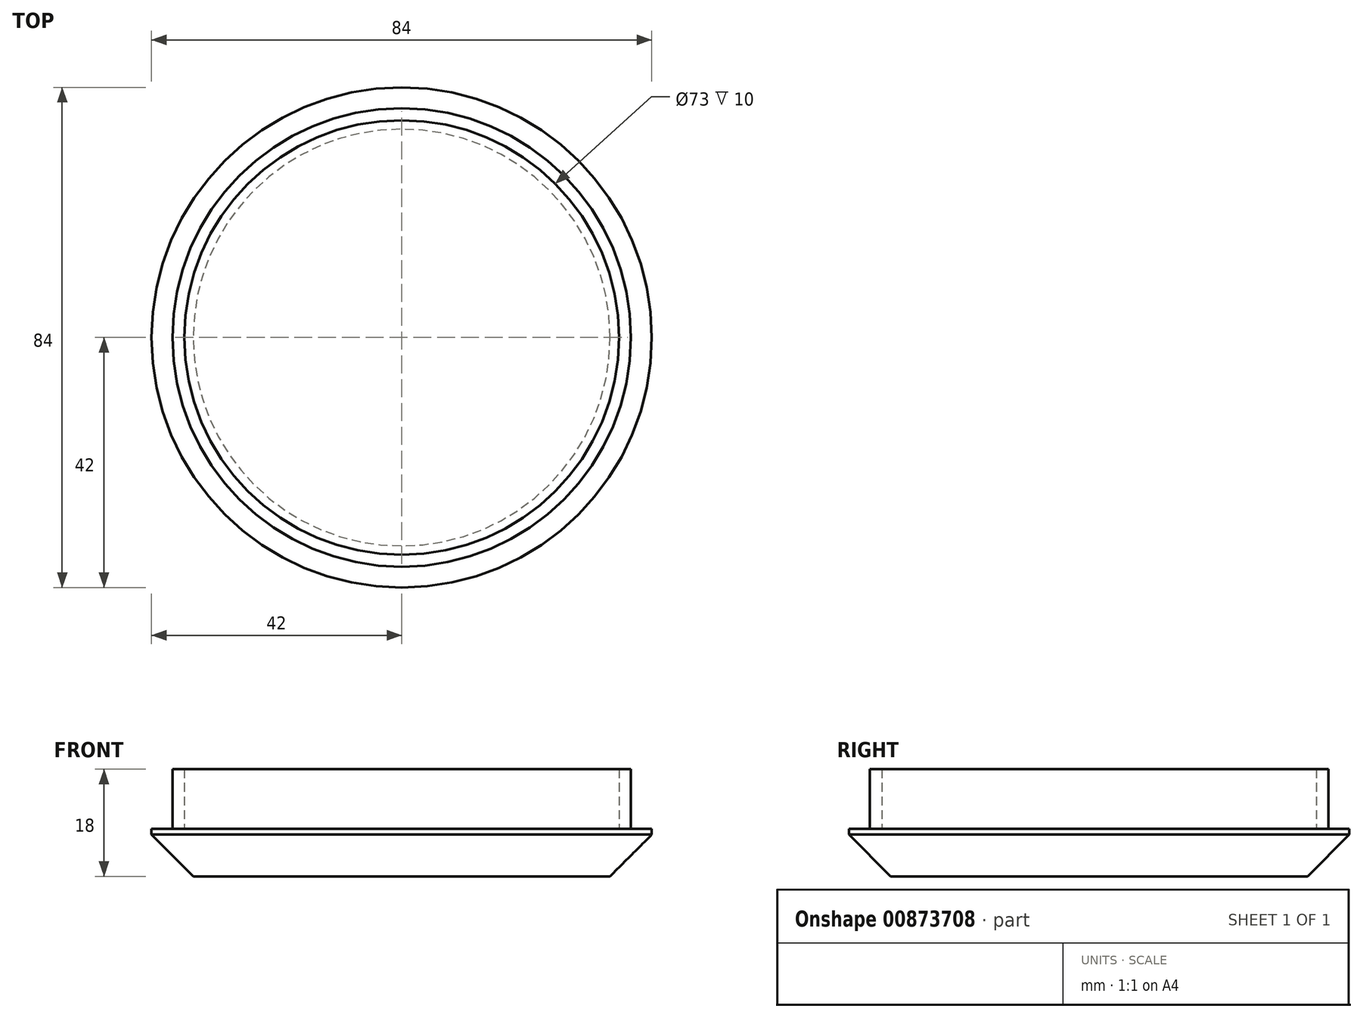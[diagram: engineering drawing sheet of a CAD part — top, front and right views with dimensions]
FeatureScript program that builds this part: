
annotation { "Feature Type Name" : "Feature", "Feature Type Description" : "" }
export const myFeature = defineFeature(function(context is Context, id is Id, definition is map)
    precondition{}
    {
        {
            var Q0;
            Q0=qCreatedBy(makeId("Top.planeOp"),FACE);
            var sketch = newSketch(context, id + "F0", { "sketchPlane" : qUnion([Q0])});
            skCircle(sketch, "E0", {"center": v(0, 0) * mm, "radius": 38.5 * mm});
            skCircle(sketch, "E1", {"center": v(0, 0) * mm, "radius": 36.5 * mm});
            skSolve(sketch);
        }
        {
            var Q0;
            Q0=makeQuery(id+"F0.imprint","IMPRINT",FACE,{"disambiguationData":[TD([[makeQuery(id+"F0.imprint","IMPRINT",EDGE,{"derivedFrom":sQuery(id+"F0.wireOp",EDGE,"E0")}),1.0]])]});
            extrude(context, id + "F1", {"entities" : qUnion([Q0]), "depth" : 10 * mm, "offsetDistance" : 25 * mm});
        }
        {
            var Q0;
            Q0=qCreatedBy(makeId("Top.planeOp"),FACE);
            var sketch = newSketch(context, id + "F2", { "sketchPlane" : qUnion([Q0])});
            skCircle(sketch, "E2", {"center": v(0, 0) * mm, "radius": 42 * mm});
            skSolve(sketch);
        }
        {
            var Q0;
            Q0=makeQuery(id+"F2.imprint","IMPRINT",FACE,{"disambiguationData":[TD([[makeQuery(id+"F2.imprint","IMPRINT",EDGE,{"derivedFrom":sQuery(id+"F2.wireOp",EDGE,"E2")}),1.0]])]});
            var Q1;
            Q1=sQuery(id+"F2.wireOp",EDGE,"E2");
            extrude(context, id + "F3", {"entities" : qUnion([Q0]), "operationType" : NewBodyOperationType.ADD, "surfaceEntities" : qUnion([Q1]), "oppositeDirection" : true, "depth" : 8 * mm, "offsetDistance" : 25 * mm});
        }
        {
            var Q0;
            Q0=makeQuery(id+"F3.opExtrude","CAP_EDGE",EDGE,{"disambiguationData":[OSD([sQuery(id+"F2.wireOp",EDGE,"E2")])],"isStart":false});
            chamfer(context, id + "F4", {"entities" : qUnion([Q0]), "width" : 7 * mm, "tangentPropagation" : true});
        }
    });
